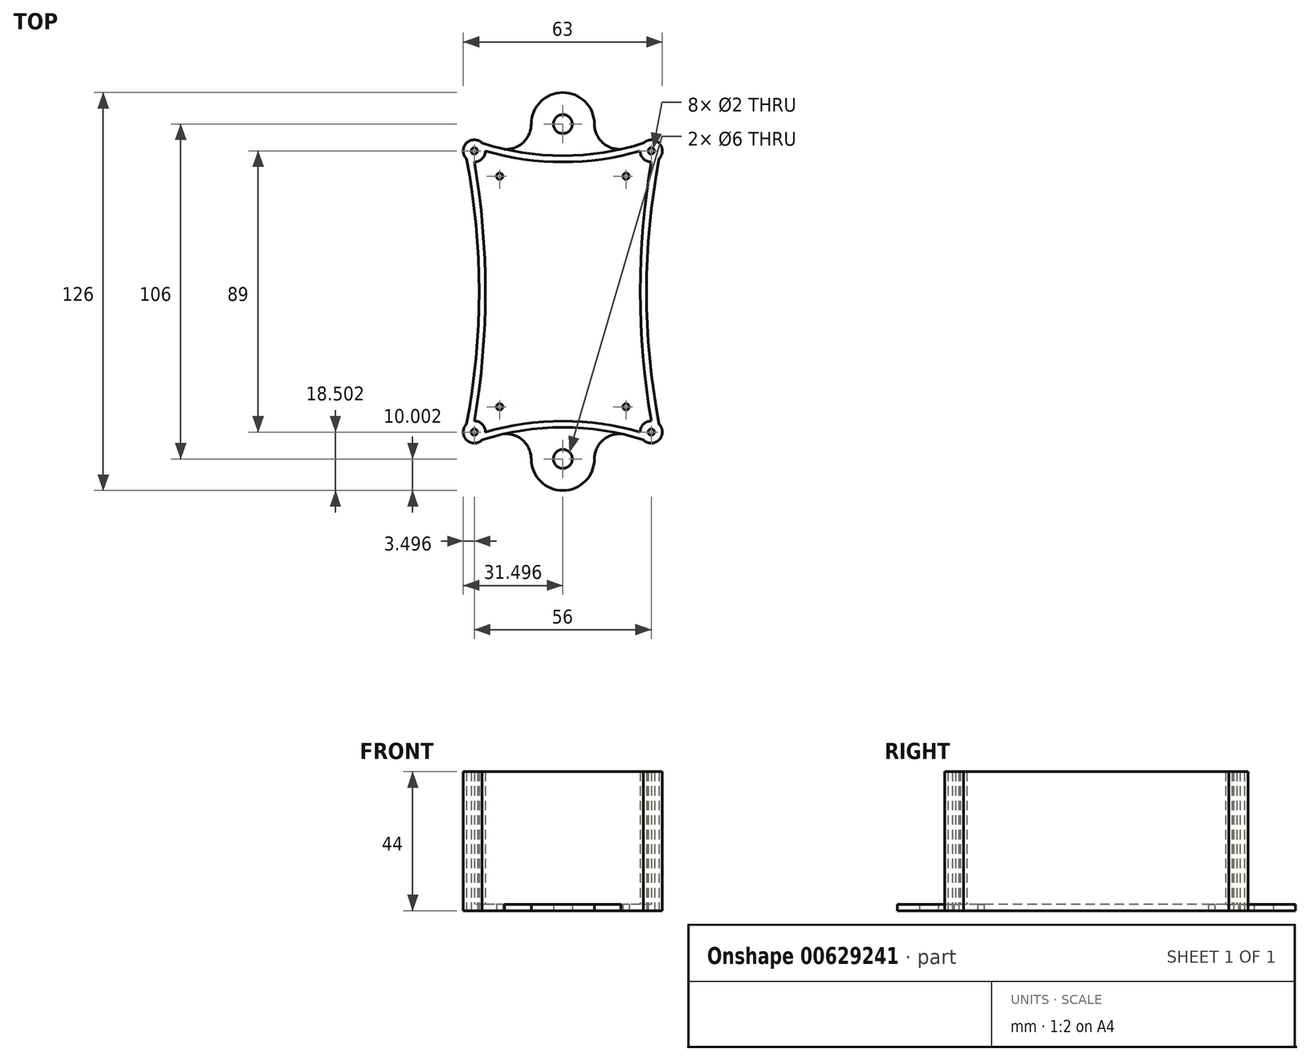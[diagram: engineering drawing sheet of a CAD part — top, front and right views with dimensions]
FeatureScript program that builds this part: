
annotation { "Feature Type Name" : "Feature", "Feature Type Description" : "" }
export const myFeature = defineFeature(function(context is Context, id is Id, definition is map)
    precondition{}
    {
        {
            var Q0;
            Q0=qCreatedBy(makeId("Top.planeOp"),FACE);
            var sketch = newSketch(context, id + "F0", { "sketchPlane" : qUnion([Q0])});
            skLineSegment(sketch, "E0", {"start": v(-67, 44.67) * mm, "end": v(-27, 44.67) * mm, "construction": true});
            skLineSegment(sketch, "E1", {"start": v(-27, 44.67) * mm, "end": v(-27, -28.33) * mm, "construction": true});
            skLineSegment(sketch, "E2", {"start": v(-27, -28.33) * mm, "end": v(-67, -28.33) * mm, "construction": true});
            skLineSegment(sketch, "E3", {"start": v(-67, -28.33) * mm, "end": v(-67, 44.67) * mm, "construction": true});
            skPoint(sketch, "E4", {"position": v(-67, 44.67) * mm});
            skPoint(sketch, "E5", {"position": v(-27, 44.67) * mm});
            skPoint(sketch, "E6", {"position": v(-27, -28.33) * mm});
            skPoint(sketch, "E7", {"position": v(-67, -28.33) * mm});
            skPoint(sketch, "E8", {"position": v(-69.5, 47.17) * mm});
            skPoint(sketch, "E9", {"position": v(-24.5, -30.83) * mm});
            skLineSegment(sketch, "E10.bottom", {"start": v(-69.5, 47.17) * mm, "end": v(-24.5, 47.17) * mm, "construction": true});
            skLineSegment(sketch, "E10.top", {"start": v(-69.5, -30.83) * mm, "end": v(-24.5, -30.83) * mm, "construction": true});
            skLineSegment(sketch, "E10.left", {"start": v(-69.5, 47.17) * mm, "end": v(-69.5, -30.83) * mm, "construction": true});
            skLineSegment(sketch, "E10.right", {"start": v(-24.5, 47.17) * mm, "end": v(-24.5, -30.83) * mm, "construction": true});
            skLineSegment(sketch, "E11", {"start": v(-69.5, 47.17) * mm, "end": v(-67, 44.67) * mm, "construction": true});
            skLineSegment(sketch, "E12", {"start": v(-27, -28.33) * mm, "end": v(-24.5, -30.83) * mm, "construction": true});
            skLineSegment(sketch, "E13", {"start": v(-67, -28.33) * mm, "end": v(-69.5, -30.83) * mm, "construction": true});
            skLineSegment(sketch, "E14", {"start": v(-27, 44.67) * mm, "end": v(-24.5, 47.17) * mm, "construction": true});
            skLineSegment(sketch, "E15.bottom", {"start": v(-69.5, 47.17) * mm, "end": v(-73.5, 47.17) * mm, "construction": true});
            skLineSegment(sketch, "E15.top", {"start": v(-69.5, 51.17) * mm, "end": v(-73.5, 51.17) * mm, "construction": true});
            skLineSegment(sketch, "E15.left", {"start": v(-69.5, 47.17) * mm, "end": v(-69.5, 51.17) * mm, "construction": true});
            skLineSegment(sketch, "E15.right", {"start": v(-73.5, 47.17) * mm, "end": v(-73.5, 51.17) * mm, "construction": true});
            skLineSegment(sketch, "E16.bottom", {"start": v(-24.5, -30.83) * mm, "end": v(-20.5, -30.83) * mm, "construction": true});
            skLineSegment(sketch, "E16.top", {"start": v(-24.5, -34.83) * mm, "end": v(-20.5, -34.83) * mm, "construction": true});
            skLineSegment(sketch, "E16.left", {"start": v(-24.5, -30.83) * mm, "end": v(-24.5, -34.83) * mm, "construction": true});
            skLineSegment(sketch, "E16.right", {"start": v(-20.5, -30.83) * mm, "end": v(-20.5, -34.83) * mm, "construction": true});
            skLineSegment(sketch, "E17", {"start": v(-73.5, 51.17) * mm, "end": v(-69.5, 47.17) * mm, "construction": true});
            skLineSegment(sketch, "E18", {"start": v(-20.5, -34.83) * mm, "end": v(-24.5, -30.83) * mm, "construction": true});
            skPoint(sketch, "E19", {"position": v(-71.5, 49.17) * mm});
            skPoint(sketch, "E20", {"position": v(-22.5, -32.83) * mm});
            skLineSegment(sketch, "E21.bottom", {"start": v(-71.5, 49.17) * mm, "end": v(-22.5, 49.17) * mm, "construction": true});
            skLineSegment(sketch, "E21.top", {"start": v(-71.5, -32.83) * mm, "end": v(-22.5, -32.83) * mm, "construction": true});
            skLineSegment(sketch, "E21.left", {"start": v(-71.5, 49.17) * mm, "end": v(-71.5, -32.83) * mm, "construction": true});
            skLineSegment(sketch, "E21.right", {"start": v(-22.5, 49.17) * mm, "end": v(-22.5, -32.83) * mm, "construction": true});
            skLineSegment(sketch, "E22.bottom", {"start": v(-71.5, 49.17) * mm, "end": v(-78.5, 49.17) * mm, "construction": true});
            skLineSegment(sketch, "E22.top", {"start": v(-71.5, 56.17) * mm, "end": v(-78.5, 56.17) * mm, "construction": true});
            skLineSegment(sketch, "E22.left", {"start": v(-71.5, 49.17) * mm, "end": v(-71.5, 56.17) * mm, "construction": true});
            skLineSegment(sketch, "E22.right", {"start": v(-78.5, 49.17) * mm, "end": v(-78.5, 56.17) * mm, "construction": true});
            skLineSegment(sketch, "E23.bottom", {"start": v(-22.5, -32.83) * mm, "end": v(-15.5, -32.83) * mm, "construction": true});
            skLineSegment(sketch, "E23.top", {"start": v(-22.5, -39.83) * mm, "end": v(-15.5, -39.83) * mm, "construction": true});
            skLineSegment(sketch, "E23.left", {"start": v(-22.5, -32.83) * mm, "end": v(-22.5, -39.83) * mm, "construction": true});
            skLineSegment(sketch, "E23.right", {"start": v(-15.5, -32.83) * mm, "end": v(-15.5, -39.83) * mm, "construction": true});
            skLineSegment(sketch, "E24.bottom", {"start": v(-78.5, -39.83) * mm, "end": v(-71.5, -39.83) * mm, "construction": true});
            skLineSegment(sketch, "E24.top", {"start": v(-78.5, -32.83) * mm, "end": v(-71.5, -32.83) * mm, "construction": true});
            skLineSegment(sketch, "E24.left", {"start": v(-78.5, -39.83) * mm, "end": v(-78.5, -32.83) * mm, "construction": true});
            skLineSegment(sketch, "E24.right", {"start": v(-71.5, -39.83) * mm, "end": v(-71.5, -32.83) * mm, "construction": true});
            skLineSegment(sketch, "E25.bottom", {"start": v(-22.5, 49.17) * mm, "end": v(-15.5, 49.17) * mm, "construction": true});
            skLineSegment(sketch, "E25.top", {"start": v(-22.5, 56.17) * mm, "end": v(-15.5, 56.17) * mm, "construction": true});
            skLineSegment(sketch, "E25.left", {"start": v(-22.5, 49.17) * mm, "end": v(-22.5, 56.17) * mm, "construction": true});
            skLineSegment(sketch, "E25.right", {"start": v(-15.5, 49.17) * mm, "end": v(-15.5, 56.17) * mm, "construction": true});
            skLineSegment(sketch, "E26", {"start": v(-78.5, 56.17) * mm, "end": v(-71.5, 49.17) * mm, "construction": true});
            skLineSegment(sketch, "E27", {"start": v(-15.5, 56.17) * mm, "end": v(-22.5, 49.17) * mm, "construction": true});
            skLineSegment(sketch, "E28", {"start": v(-78.5, -39.83) * mm, "end": v(-71.5, -32.83) * mm, "construction": true});
            skLineSegment(sketch, "E29", {"start": v(-15.5, -39.83) * mm, "end": v(-22.5, -32.83) * mm, "construction": true});
            skPoint(sketch, "E30", {"position": v(-75, 52.67) * mm});
            skPoint(sketch, "E31", {"position": v(-19, 52.67) * mm});
            skPoint(sketch, "E32", {"position": v(-19, -36.33) * mm});
            skPoint(sketch, "E33", {"position": v(-75, -36.33) * mm});
            skCircle(sketch, "E34", {"center": v(-67, 44.67) * mm, "radius": 1 * mm});
            skCircle(sketch, "E35", {"center": v(-27, 44.67) * mm, "radius": 1 * mm});
            skCircle(sketch, "E36", {"center": v(-27, -28.33) * mm, "radius": 1 * mm});
            skCircle(sketch, "E37", {"center": v(-67, -28.33) * mm, "radius": 1 * mm});
            skCircle(sketch, "E38", {"center": v(-75, 52.67) * mm, "radius": 1 * mm});
            skCircle(sketch, "E39", {"center": v(-19, 52.67) * mm, "radius": 1 * mm});
            skCircle(sketch, "E40", {"center": v(-19, -36.33) * mm, "radius": 1 * mm});
            skCircle(sketch, "E41", {"center": v(-75, -36.33) * mm, "radius": 1 * mm});
            skPoint(sketch, "E42", {"position": v(-47, 49.17) * mm});
            skPoint(sketch, "E43", {"position": v(-47, -32.83) * mm});
            skPoint(sketch, "E44", {"position": v(-71.5, -36.33) * mm});
            skPoint(sketch, "E45", {"position": v(-75, -32.83) * mm});
            skPoint(sketch, "E46", {"position": v(-75, 49.17) * mm});
            skPoint(sketch, "E47", {"position": v(-71.5, 52.67) * mm});
            skPoint(sketch, "E48", {"position": v(-22.5, 52.67) * mm});
            skPoint(sketch, "E49", {"position": v(-19, 49.17) * mm});
            skPoint(sketch, "E50", {"position": v(-19, -32.83) * mm});
            skPoint(sketch, "E51", {"position": v(-22.5, -36.33) * mm});
            skPoint(sketch, "E52", {"position": v(-71.5, 8.17) * mm});
            skLineSegment(sketch, "E53", {"start": v(-78.5, 49.17) * mm, "end": v(-71.5, 56.17) * mm, "construction": true});
            skLineSegment(sketch, "E54", {"start": v(-22.5, 56.17) * mm, "end": v(-15.5, 49.17) * mm, "construction": true});
            skLineSegment(sketch, "E55", {"start": v(-22.5, -39.83) * mm, "end": v(-15.5, -32.83) * mm, "construction": true});
            skLineSegment(sketch, "E56", {"start": v(-71.5, -39.83) * mm, "end": v(-78.5, -32.83) * mm, "construction": true});
            skPoint(sketch, "E57", {"position": v(-77.47, 50.2) * mm});
            skPoint(sketch, "E58", {"position": v(-72.52, 55.15) * mm});
            skPoint(sketch, "E59", {"position": v(-16.52, 50.2) * mm});
            skPoint(sketch, "E60", {"position": v(-21.47, 55.15) * mm});
            skPoint(sketch, "E61", {"position": v(-16.52, -33.85) * mm});
            skPoint(sketch, "E62", {"position": v(-21.47, -38.8) * mm});
            skPoint(sketch, "E63", {"position": v(-72.52, -38.8) * mm});
            skPoint(sketch, "E64", {"position": v(-77.47, -33.85) * mm});
            skPoint(sketch, "E65", {"position": v(-22.5, 8.17) * mm});
            skLineSegment(sketch, "E66", {"start": v(-47, 49.17) * mm, "end": v(-47, 51.17) * mm, "construction": true});
            skLineSegment(sketch, "E67", {"start": v(-22.5, 8.17) * mm, "end": v(-20.5, 8.17) * mm, "construction": true});
            skLineSegment(sketch, "E68", {"start": v(-47, -32.83) * mm, "end": v(-47, -34.83) * mm, "construction": true});
            skLineSegment(sketch, "E69", {"start": v(-71.5, 8.17) * mm, "end": v(-73.5, 8.17) * mm, "construction": true});
            skArc(sketch, "E70", {"start": v(-77.47, -33.85) * mm, "mid": v(-73.5, 8.17) * mm, "end": v(-77.47, 50.2) * mm});
            skArc(sketch, "E71", {"start": v(-21.47, -38.8) * mm, "mid": v(-47, -34.83) * mm, "end": v(-72.52, -38.8) * mm});
            skArc(sketch, "E72", {"start": v(-16.52, 50.2) * mm, "mid": v(-20.5, 8.17) * mm, "end": v(-16.52, -33.85) * mm});
            skArc(sketch, "E73", {"start": v(-71.5, 52.67) * mm, "mid": v(-47, 49.17) * mm, "end": v(-22.5, 52.67) * mm});
            skArc(sketch, "E74", {"start": v(-19, 49.17) * mm, "mid": v(-22.5, 8.17) * mm, "end": v(-19, -32.83) * mm});
            skArc(sketch, "E75", {"start": v(-75, -32.83) * mm, "mid": v(-71.5, 8.17) * mm, "end": v(-75, 49.17) * mm});
            skArc(sketch, "E76", {"start": v(-22.5, -36.33) * mm, "mid": v(-47, -32.83) * mm, "end": v(-71.5, -36.33) * mm});
            skArc(sketch, "E77", {"start": v(-75, -32.83) * mm, "mid": v(-72.52, -33.85) * mm, "end": v(-71.5, -36.33) * mm});
            skArc(sketch, "E78", {"start": v(-77.47, -33.85) * mm, "mid": v(-77.47, -38.8) * mm, "end": v(-72.52, -38.8) * mm});
            skArc(sketch, "E79", {"start": v(-19, -32.83) * mm, "mid": v(-21.47, -33.85) * mm, "end": v(-22.5, -36.33) * mm});
            skArc(sketch, "E80", {"start": v(-16.52, -33.85) * mm, "mid": v(-16.52, -38.8) * mm, "end": v(-21.47, -38.8) * mm});
            skArc(sketch, "E81", {"start": v(-21.47, 55.15) * mm, "mid": v(-16.52, 55.15) * mm, "end": v(-16.52, 50.2) * mm});
            skArc(sketch, "E82", {"start": v(-22.5, 52.67) * mm, "mid": v(-21.47, 50.2) * mm, "end": v(-19, 49.17) * mm});
            skArc(sketch, "E83", {"start": v(-72.52, 55.15) * mm, "mid": v(-77.47, 55.15) * mm, "end": v(-77.47, 50.2) * mm});
            skArc(sketch, "E84", {"start": v(-71.5, 52.67) * mm, "mid": v(-72.52, 50.2) * mm, "end": v(-75, 49.17) * mm});
            skPoint(sketch, "E85", {"position": v(-47, 51.17) * mm});
            skArc(sketch, "E86", {"start": v(-72.52, 55.15) * mm, "mid": v(-47, 51.17) * mm, "end": v(-21.47, 55.15) * mm});
            skLineSegment(sketch, "E87", {"start": v(-47, 51.17) * mm, "end": v(-47, 71.17) * mm, "construction": true});
            skLineSegment(sketch, "E88", {"start": v(-47, 71.17) * mm, "end": v(-37, 71.17) * mm, "construction": true});
            skLineSegment(sketch, "E89", {"start": v(-37, 71.17) * mm, "end": v(-37, 51.77) * mm, "construction": true});
            skLineSegment(sketch, "E90", {"start": v(-47, 71.17) * mm, "end": v(-57, 71.17) * mm, "construction": true});
            skLineSegment(sketch, "E91", {"start": v(-57, 71.17) * mm, "end": v(-57, 51.77) * mm, "construction": true});
            skPoint(sketch, "E92", {"position": v(-57, 51.77) * mm});
            skPoint(sketch, "E93", {"position": v(-47, 71.17) * mm});
            skPoint(sketch, "E94", {"position": v(-37, 51.77) * mm});
            skPoint(sketch, "E95", {"position": v(-47, 61.17) * mm});
            skCircle(sketch, "E96", {"center": v(-47, 61.17) * mm, "radius": 3 * mm});
            skCircle(sketch, "E97", {"center": v(-47, 61.17) * mm, "radius": 10 * mm, "construction": true});
            skPoint(sketch, "E98", {"position": v(-57, 61.17) * mm});
            skPoint(sketch, "E99", {"position": v(-37, 61.17) * mm});
            skArc(sketch, "E100", {"start": v(-57, 61.17) * mm, "mid": v(-47, 71.17) * mm, "end": v(-37, 61.17) * mm});
            skPoint(sketch, "E101", {"position": v(-65.43, 53.22) * mm});
            skArc(sketch, "E102", {"start": v(-65.43, 53.22) * mm, "mid": v(-59.5, 55.39) * mm, "end": v(-57, 61.17) * mm});
            skLineSegment(sketch, "E103", {"start": v(-67, 44.67) * mm, "end": v(-27, -28.33) * mm, "construction": true});
            skLineSegment(sketch, "E104", {"start": v(-67, -28.33) * mm, "end": v(-27, 44.67) * mm, "construction": true});
            skPoint(sketch, "E105", {"position": v(-47, 8.17) * mm});
            skCircle(sketch, "E106", {"center": v(-47, 8.17) * mm, "radius": 48.68 * mm, "construction": true});
            skPoint(sketch, "E107", {"position": v(-28.55, 53.22) * mm});
            skPoint(sketch, "E108", {"position": v(-28.55, -36.88) * mm});
            skPoint(sketch, "E109", {"position": v(-65.43, -36.88) * mm});
            skArc(sketch, "E110", {"start": v(-37, 61.17) * mm, "mid": v(-34.48, 55.39) * mm, "end": v(-28.55, 53.22) * mm});
            skLineSegment(sketch, "E111", {"start": v(-47, -34.83) * mm, "end": v(-47, -54.83) * mm, "construction": true});
            skLineSegment(sketch, "E112", {"start": v(-47, -54.83) * mm, "end": v(-57, -54.83) * mm, "construction": true});
            skLineSegment(sketch, "E113", {"start": v(-57, -54.83) * mm, "end": v(-57, -35.43) * mm, "construction": true});
            skLineSegment(sketch, "E114", {"start": v(-47, -54.83) * mm, "end": v(-37, -54.83) * mm, "construction": true});
            skLineSegment(sketch, "E115", {"start": v(-37, -54.83) * mm, "end": v(-37, -35.43) * mm, "construction": true});
            skPoint(sketch, "E116", {"position": v(-47, -44.83) * mm});
            skCircle(sketch, "E117", {"center": v(-47, -44.83) * mm, "radius": 3 * mm});
            skArc(sketch, "E118", {"start": v(-37, -44.83) * mm, "mid": v(-47, -54.83) * mm, "end": v(-57, -44.83) * mm});
            skArc(sketch, "E119", {"start": v(-57, -44.83) * mm, "mid": v(-59.5, -39.04) * mm, "end": v(-65.43, -36.88) * mm});
            skArc(sketch, "E120", {"start": v(-28.55, -36.88) * mm, "mid": v(-34.48, -39.04) * mm, "end": v(-37, -44.83) * mm});
            skSolve(sketch);
        }
        {
            var Q0;
            Q0=makeQuery(id+"F0.imprint","IMPRINT",FACE,{"disambiguationData":[TD([[makeQuery(id+"F0.imprint","IMPRINT",EDGE,{"derivedFrom":sQuery(id+"F0.wireOp",EDGE,"E38")}),-1.0]])]});
            extrude(context, id + "F1", {"entities" : qUnion([Q0]), "depth" : 44 * mm, "offsetDistance" : 25 * mm});
        }
        {
            var Q0;
            Q0=makeQuery(id+"F0.imprint","IMPRINT",FACE,{"disambiguationData":[TD([[makeQuery(id+"F0.imprint","IMPRINT",EDGE,{"derivedFrom":sQuery(id+"F0.wireOp",EDGE,"E117")}),-1.0]])]});
            var Q1;
            Q1=makeQuery(id+"F0.imprint","IMPRINT",FACE,{"disambiguationData":[TD([[makeQuery(id+"F0.imprint","IMPRINT",EDGE,{"derivedFrom":sQuery(id+"F0.wireOp",EDGE,"E96")}),-1.0]])]});
            var Q2;
            Q2=makeQuery(id+"F0.imprint","IMPRINT",FACE,{"disambiguationData":[TD([[makeQuery(id+"F0.imprint","IMPRINT",EDGE,{"derivedFrom":sQuery(id+"F0.wireOp",EDGE,"E34")}),-1.0]])]});
            extrude(context, id + "F2", {"entities" : qUnion([Q0, Q1, Q2]), "operationType" : NewBodyOperationType.ADD, "depth" : 2 * mm, "offsetDistance" : 25 * mm});
        }
    });
